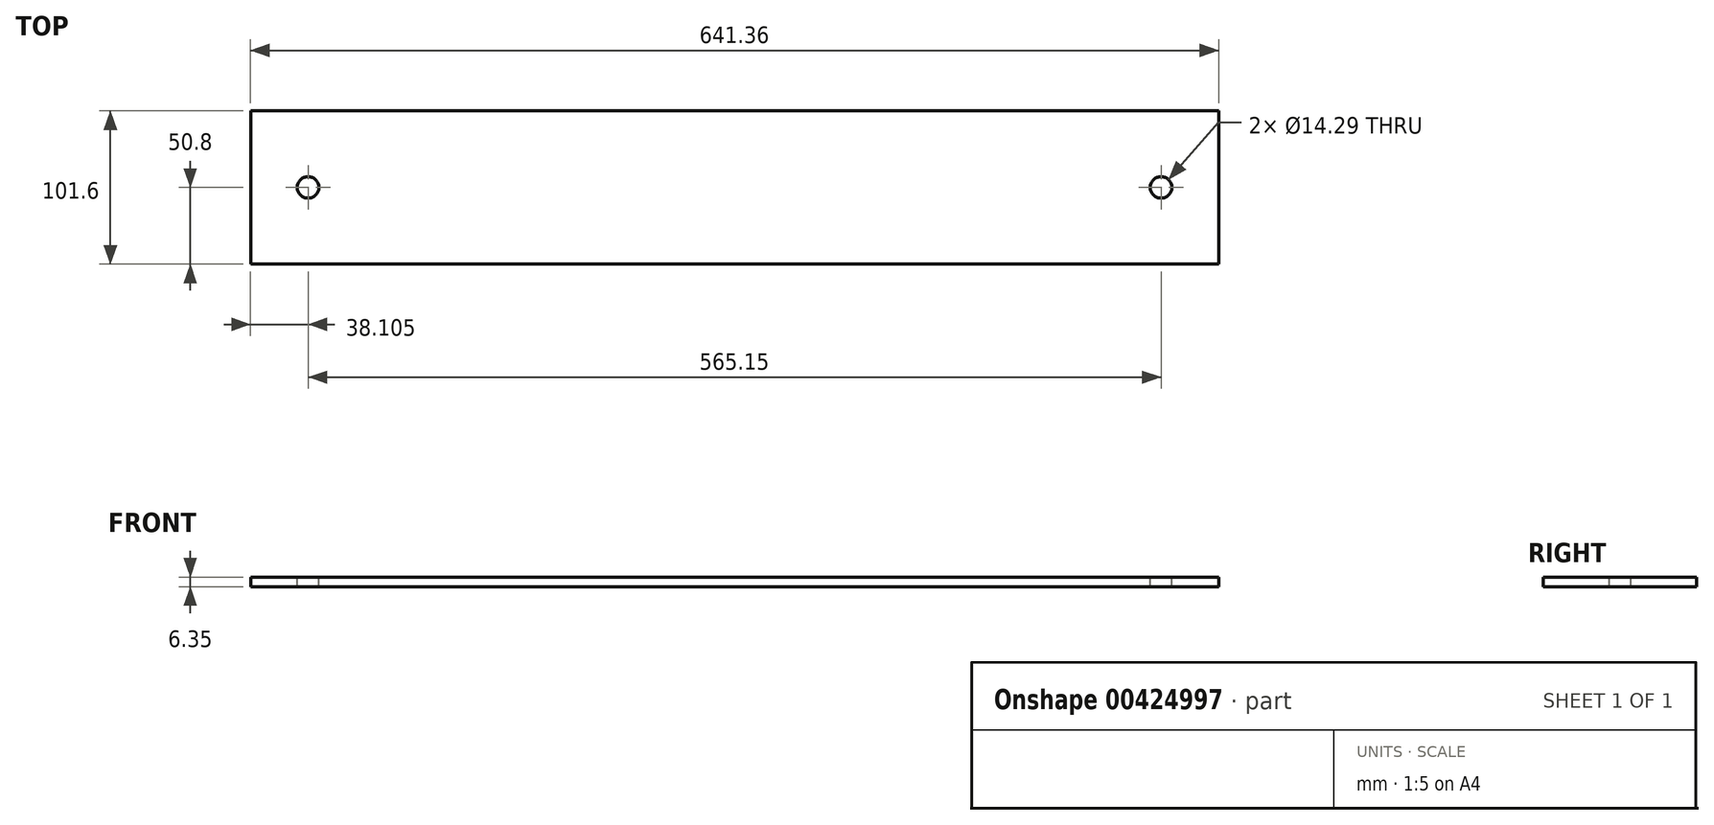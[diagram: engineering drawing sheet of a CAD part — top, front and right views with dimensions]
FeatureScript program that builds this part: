
annotation { "Feature Type Name" : "Feature", "Feature Type Description" : "" }
export const myFeature = defineFeature(function(context is Context, id is Id, definition is map)
    precondition{}
    {
        {
            var Q0;
            Q0=qCreatedBy(makeId("Top.planeOp"),FACE);
            var sketch = newSketch(context, id + "F0", { "sketchPlane" : qUnion([Q0])});
            skLineSegment(sketch, "E0.bottom", {"start": v(320.68, -50.8) * mm, "end": v(-320.67, -50.8) * mm});
            skLineSegment(sketch, "E0.top", {"start": v(320.68, 50.8) * mm, "end": v(-320.67, 50.8) * mm});
            skLineSegment(sketch, "E0.left", {"start": v(320.68, -50.8) * mm, "end": v(320.68, 50.8) * mm});
            skLineSegment(sketch, "E0.right", {"start": v(-320.67, -50.8) * mm, "end": v(-320.67, 50.8) * mm});
            skPoint(sketch, "E0.middle", {"position": v(0, 0) * mm});
            skSolve(sketch);
        }
        {
            var Q0;
            Q0 = qSketchRegion(id + "F0", true);
            extrude(context, id + "F1", {"entities" : qUnion([Q0]), "depth" : 6.35 * mm});
        }
        {
            var Q0;
            Q0=makeQuery(id+"F1.opExtrude","CAP_FACE",FACE,{"disambiguationData":[OSD([sQuery(id+"F0.wireOp",EDGE,"E0.bottom"),sQuery(id+"F0.wireOp",EDGE,"E0.top"),sQuery(id+"F0.wireOp",EDGE,"E0.left"),sQuery(id+"F0.wireOp",EDGE,"E0.right")])],"isStart":false});
            var sketch = newSketch(context, id + "F2", { "sketchPlane" : qUnion([Q0])});
            skCircle(sketch, "E1", {"center": v(-282.57, 0) * mm, "radius": 7.14 * mm});
            skCircle(sketch, "E2.MirrorC", {"center": v(282.57, 0) * mm, "radius": 7.14 * mm});
            skSolve(sketch);
        }
        {
            var Q0;
            Q0 = qSketchRegion(id + "F2", true);
            extrude(context, id + "F3", {"entities" : qUnion([Q0]), "operationType" : NewBodyOperationType.REMOVE, "oppositeDirection" : true, "depth" : 25.4 * mm});
        }
    });
